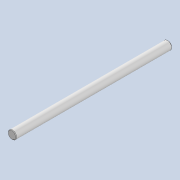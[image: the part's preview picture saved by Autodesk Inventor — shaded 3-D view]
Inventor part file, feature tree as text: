
AUTODESK INVENTOR PART (.ipt)
format: ipt  version: 2020 (Build 240168000, 168)  size: 77,824 bytes
history: native  units: mm
features: extrude x1, chamfer x1, sketch x1
ambient origin geometry x8: Origin, YZ Plane, XZ Plane, XY Plane, X Axis, Y Axis, Z Axis, Center Point
bodies: Solid1 (feature_tree)
feature tree (3):
  extrude  "Extrusion1"  Depth=150.0mm TaperAngle=0.0deg
  chamfer  "Chamfer1"  Distance=0.5mm Angle=45.0deg
  sketch  "Sketch1"  dims[d0=8.0mm d1=150.0mm d2=0.0mm d3=0.5mm d4=2.0mm d5=45.0deg]
